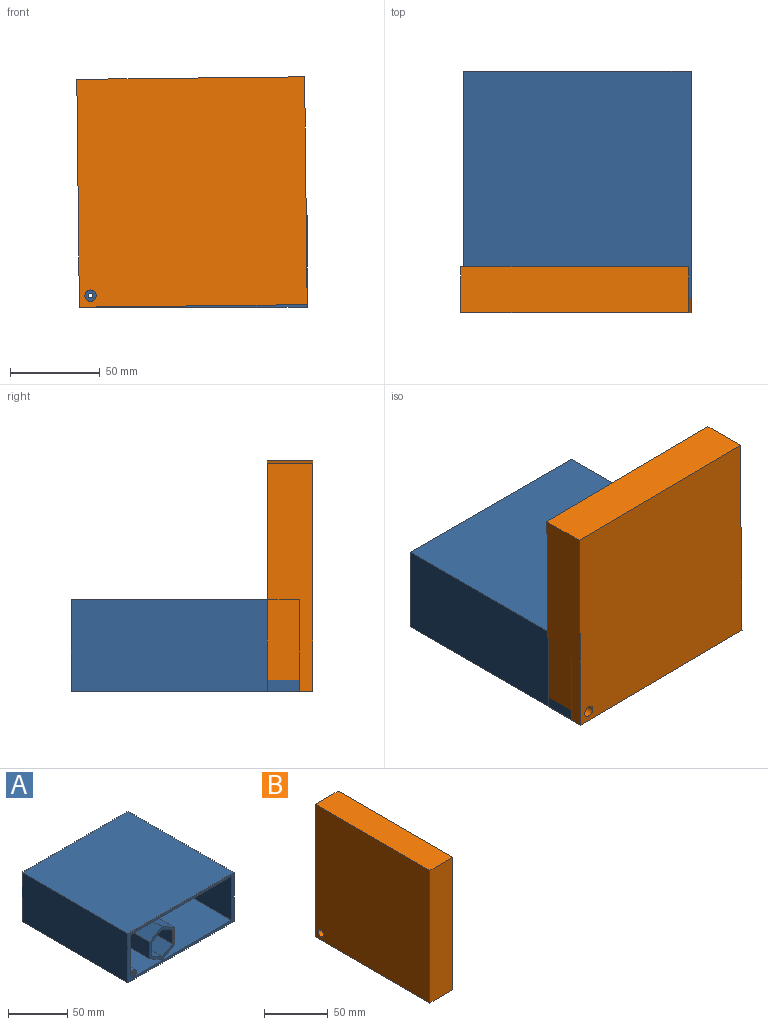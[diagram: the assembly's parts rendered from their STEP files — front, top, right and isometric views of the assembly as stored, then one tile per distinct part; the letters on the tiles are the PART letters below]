
ASSEMBLY  parts=2 mates=1
PART A: 26 faces, bbox 127x127x50.8 mm
  f0: plane 34.63x30.12mm, normal (0,-1,0), area 241.5mm2, adj f4,f5,f6,f7,f8,f9,f18,f19
  f1: plane 127x127mm, normal (0,0,1), area 16129mm2, adj f2,f11,f12,f13
  f2: plane 127x50.8mm, normal (-1,0,0), area 6451.6mm2, adj f1,f3,f12,f13
  f3: plane 127x127mm, normal (0,0,-1), area 16129mm2, adj f2,f11,f12,f13
  f4: plane 127x12.51mm, normal (-0.49,0,-0.87), area 1826.3mm2, adj f0,f5,f9,f13
  f5: plane 127x14.38mm, normal (-1,0,-0.01), area 1826.3mm2, adj f0,f4,f6,f13
  f6: plane 127x12.4mm, normal (-0.51,0,0.86), area 1826.3mm2, adj f0,f5,f7,f13
  f7: plane 127x12.51mm, normal (0.49,0,0.87), area 1826.3mm2, adj f0,f6,f8,f13
  f8: plane 127x14.38mm, normal (1,0,0.01), area 1826.3mm2, adj f0,f7,f9,f13
  f9: plane 127x12.4mm, normal (0.51,0,-0.86), area 1826.3mm2, adj f0,f4,f8,f13
  f10: cylinder r=1.27mm len=127mm, axis (0,1,0), area 1013.4mm2, adj f12,f13
  f11: plane 127x50.8mm, normal (1,0,0), area 6451.6mm2, adj f1,f3,f12,f13
  f12: plane 127x50.8mm, normal (0,-1,0), area 921.1mm2, adj f1,f2,f3,f10,f11,f14,f15,f16
  f13: plane 127x50.8mm, normal (0,1,0), area 5909.3mm2, adj f1,f2,f3,f4,f5,f6,f7,f8
  f14: cylinder r=3.81mm len=124.46mm, axis (0,1,0), area 2234.6mm2, adj f12,f15,f16,f25
  f15: plane 124.46x118.11mm, normal (0,0,1), area 14700mm2, adj f12,f14,f24,f25
  f16: plane 124.46x41.91mm, normal (1,0,0), area 5216.1mm2, adj f12,f14,f17,f25
  f17: plane 124.46x121.92mm, normal (0,0,-1), area 15174.2mm2, adj f12,f16,f24,f25
  f18: plane 124.46x15.06mm, normal (0.49,0,0.87), area 2154.8mm2, adj f0,f19,f23,f25
  f19: plane 124.46x17.31mm, normal (1,0,0.01), area 2154.8mm2, adj f0,f18,f20,f25
  f20: plane 124.46x14.93mm, normal (0.51,0,-0.86), area 2154.8mm2, adj f0,f19,f21,f25
  f21: plane 124.46x15.06mm, normal (-0.49,0,-0.87), area 2154.8mm2, adj f0,f20,f22,f25
  f22: plane 124.46x17.31mm, normal (-1,0,-0.01), area 2154.8mm2, adj f0,f21,f23,f25
  f23: plane 124.46x14.93mm, normal (-0.51,0,0.86), area 2154.8mm2, adj f0,f18,f22,f25
  f24: plane 124.46x45.72mm, normal (-1,0,0), area 5690.3mm2, adj f12,f15,f17,f25
  f25: plane 121.92x45.72mm, normal (0,-1,0), area 4746.7mm2, adj f14,f15,f16,f17,f18,f19,f20,f21
PART B: 7 faces, bbox 25.4x127x127 mm
  f0: plane 127x25.4mm, normal (0,0,1), area 3225.8mm2, adj f1,f3,f4,f5
  f1: plane 127x127mm, normal (-1,0,0), area 16097.3mm2, adj f0,f2,f4,f5,f6
  f2: plane 127x25.4mm, normal (0,0,-1), area 3225.8mm2, adj f1,f3,f4,f5
  f3: plane 127x127mm, normal (1,0,0), area 16097.3mm2, adj f0,f2,f4,f5,f6
  f4: plane 127x25.4mm, normal (0,-1,0), area 3225.8mm2, adj f0,f1,f2,f3
  f5: plane 127x25.4mm, normal (0,1,0), area 3225.8mm2, adj f0,f1,f2,f3
  f6: cylinder r=3.17mm len=25.4mm, axis (-1,0,0), area 506.7mm2, adj f1,f3
PLACE A t=(-2.73,0,16.62)mm
PLACE B rot(axis=(-0.58,0.58,-0.58),119.6deg) t=(30.81,-147.15,-50.98)mm
MATE cylindrical B.f6 <-> A.f10  axis (0,-1,0) through (-48.01,-134.64,-45.5)mm
